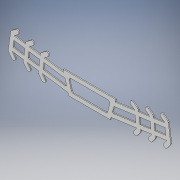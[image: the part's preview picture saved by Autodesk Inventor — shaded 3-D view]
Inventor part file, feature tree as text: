
AUTODESK INVENTOR PART (.ipt)
format: ipt  version: 2019 (Build 230136000, 136)  size: 313,344 bytes
history: native  units: mm
features: extrude x4, sketch x2, fillet x2, other x1, pattern_linear x1, mirror x1, projected_geometry x1
ambient origin geometry x8: Origin, YZ Plane, XZ Plane, XY Plane, X Axis, Y Axis, Z Axis, Center Point
bodies: Solid2 (feature_tree)
feature tree (12):
  sketch  "Sketch2"  dims[d2=12.4mm d16=12.4mm]
  extrude  "Extrusion2"  Depth=12.4mm
  extrude  "Extrusion3"  Depth=4.0mm
  extrude  "Extrusion4"  Depth=1.0mm TaperAngle=0.0deg
  extrude  "Extrusion6"  Depth=4.0mm
  fillet  "Fillet2"  Radius=2.0mm
  fillet  "Fillet4"  Radius=1.0mm
  other  "Work Axis1"
  pattern_linear  "Rectangular Pattern1"  Spacing1=4.0mm  [1 undecoded]
  mirror  "Mirror2"
  sketch  "Sketch3"  dims[d28=14.3117mm d30=80.0mm d31=1.0mm d32=0.0mm d33=4.0mm d34=2.0mm d35=1.0mm d36=0.0mm d37=4.0mm d39=4.0mm d40=5.0mm d41=1.0mm d42=0.0mm d48=4.0mm d49=2.0mm d52=1.0mm d53=30.0mm d55=15.0mm d58=2.5mm d59=26.0mm d60=105.0deg d61=1.0mm d62=0.0mm d63=2.5mm d64=20.0mm d67=4.0mm d68=0.5mm]
  projected_geometry  "Projected Loop1"
note: 1 required parameter value undecoded (feature->parameter linkage not recoverable at this tier; creation-order binding heuristic only, values carry confidence <= 0.55)
